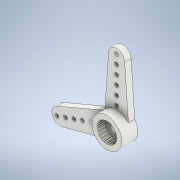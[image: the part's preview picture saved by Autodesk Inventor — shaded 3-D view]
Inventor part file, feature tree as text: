
AUTODESK INVENTOR PART (.ipt)
format: ipt  version: 2022 (Build 260153000, 153)  size: 230,912 bytes
history: mixed  units: in
note: dims shown in document units (in); Inventor stores cm internally (conversion verified against a paired STEP export)
features: sketch x3, pattern_circular x1, imported_body x1
ambient origin geometry x8: Origin, YZ Plane, XZ Plane, XY Plane, X Axis, Y Axis, Z Axis, Center Point
bodies: Solid1 (imported_parasolid), Body1 (imported_parasolid)
feature tree (5):
  sketch  "스케치1"
  sketch  "스케치2"
  pattern_circular  "원형 패턴1"  Count=2  [1 undecoded]
  sketch  "스케치4"
  imported_body  NMx_Import_Brep_tag  [imported B-rep: ~115 faces, bbox_mm=[16.707081, 21.156353, 3.8]]
note: 1 required parameter value undecoded (feature->parameter linkage not recoverable at this tier; creation-order binding heuristic only, values carry confidence <= 0.55)
